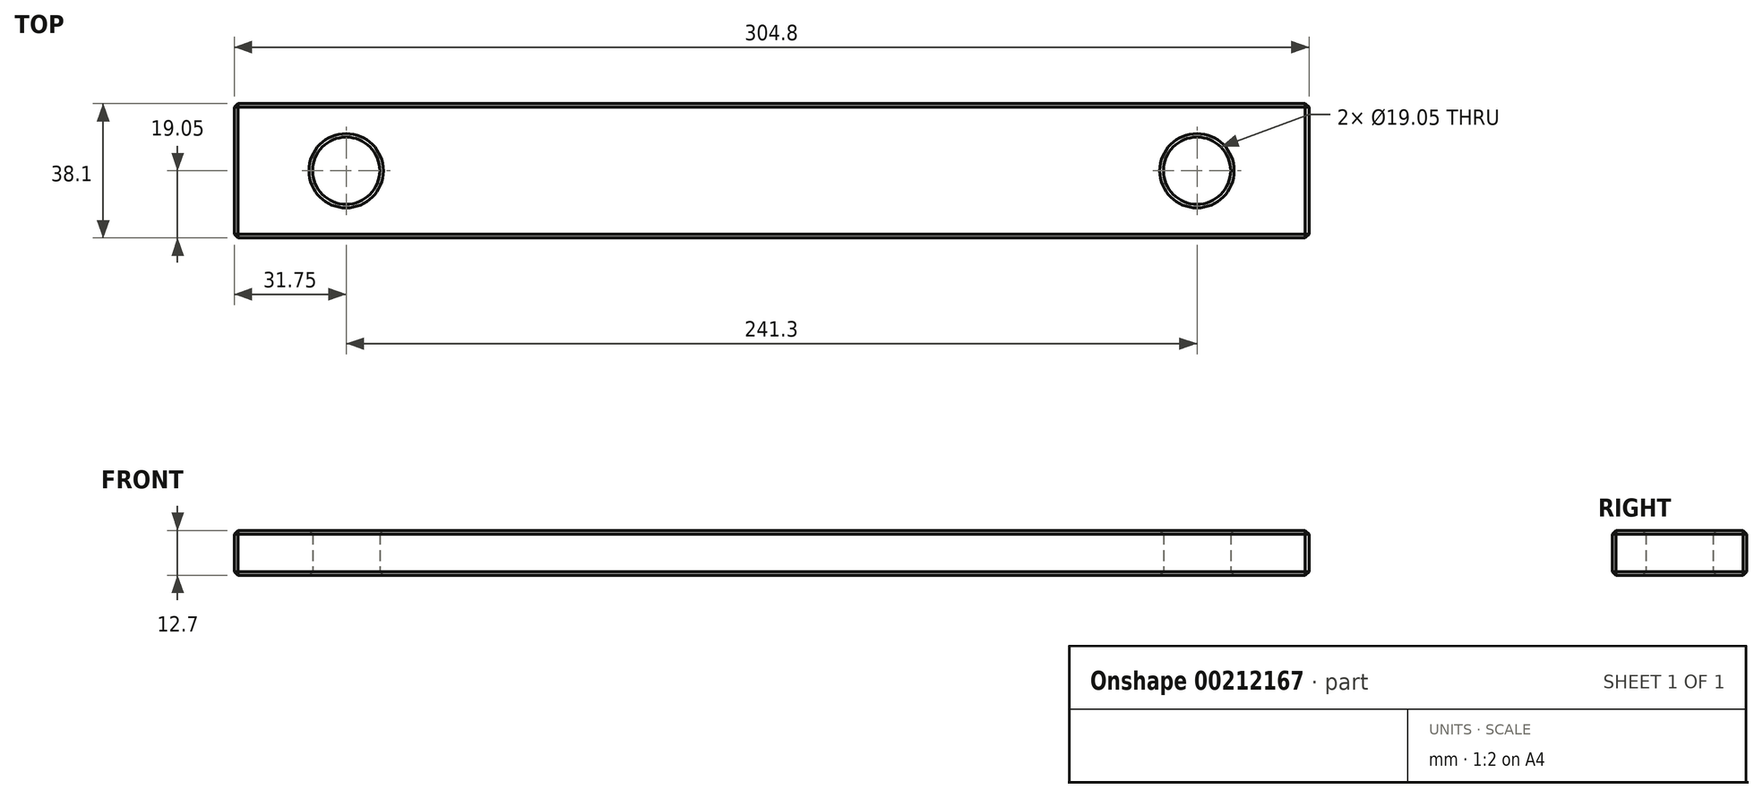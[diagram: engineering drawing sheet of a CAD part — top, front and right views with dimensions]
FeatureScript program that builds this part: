
annotation { "Feature Type Name" : "Feature", "Feature Type Description" : "" }
export const myFeature = defineFeature(function(context is Context, id is Id, definition is map)
    precondition{}
    {
        {
            var Q0;
            Q0=qCreatedBy(makeId("Top.planeOp"),FACE);
            var sketch = newSketch(context, id + "F0", { "sketchPlane" : qUnion([Q0])});
            skLineSegment(sketch, "E0.bottom", {"start": v(-152.4, 19.05) * mm, "end": v(152.4, 19.05) * mm});
            skLineSegment(sketch, "E0.top", {"start": v(-152.4, -19.05) * mm, "end": v(152.4, -19.05) * mm});
            skLineSegment(sketch, "E0.left", {"start": v(-152.4, 19.05) * mm, "end": v(-152.4, -19.05) * mm});
            skLineSegment(sketch, "E0.right", {"start": v(152.4, 19.05) * mm, "end": v(152.4, -19.05) * mm});
            skPoint(sketch, "E0.middle", {"position": v(0, 0) * mm});
            skCircle(sketch, "E1", {"center": v(-120.65, 0) * mm, "radius": 9.53 * mm});
            skCircle(sketch, "E2", {"center": v(120.65, 0) * mm, "radius": 9.53 * mm});
            skLineSegment(sketch, "E3", {"start": v(0, 0) * mm, "end": v(-120.65, 0) * mm, "construction": true});
            skLineSegment(sketch, "E4", {"start": v(0, 0) * mm, "end": v(120.65, 0) * mm, "construction": true});
            skSolve(sketch);
        }
        {
            var Q0;
            Q0=makeQuery(id+"F0.imprint","IMPRINT",FACE,{"disambiguationData":[TD([[makeQuery(id+"F0.imprint","IMPRINT",EDGE,{"derivedFrom":sQuery(id+"F0.wireOp",EDGE,"E0.bottom")}),-1.0]])]});
            extrude(context, id + "F1", {"entities" : qUnion([Q0]), "depth" : 12.7 * mm});
        }
        {
            var Q0;
            Q0=makeQuery(id+"F1.opExtrude","CAP_FACE",FACE,{"disambiguationData":[OSD([sQuery(id+"F0.wireOp",EDGE,"E0.bottom"),sQuery(id+"F0.wireOp",EDGE,"E0.top"),sQuery(id+"F0.wireOp",EDGE,"E0.left"),sQuery(id+"F0.wireOp",EDGE,"E0.right"),sQuery(id+"F0.wireOp",EDGE,"E1"),sQuery(id+"F0.wireOp",EDGE,"E2")])],"isStart":true});
            var Q1;
            Q1=makeQuery(id+"F1.opExtrude","SWEPT_FACE",FACE,{"disambiguationData":[OSD([sQuery(id+"F0.wireOp",EDGE,"E0.right")])]});
            var Q2;
            Q2=makeQuery(id+"F1.opExtrude","CAP_FACE",FACE,{"disambiguationData":[OSD([sQuery(id+"F0.wireOp",EDGE,"E0.bottom"),sQuery(id+"F0.wireOp",EDGE,"E0.top"),sQuery(id+"F0.wireOp",EDGE,"E0.left"),sQuery(id+"F0.wireOp",EDGE,"E0.right"),sQuery(id+"F0.wireOp",EDGE,"E1"),sQuery(id+"F0.wireOp",EDGE,"E2")])],"isStart":false});
            var Q3;
            Q3=makeQuery(id+"F1.opExtrude","SWEPT_FACE",FACE,{"disambiguationData":[OSD([sQuery(id+"F0.wireOp",EDGE,"E0.left")])]});
            chamfer(context, id + "F2", {"entities" : qUnion([Q0, Q1, Q2, Q3]), "width" : 1.02 * mm, "tangentPropagation" : true});
        }
    });
